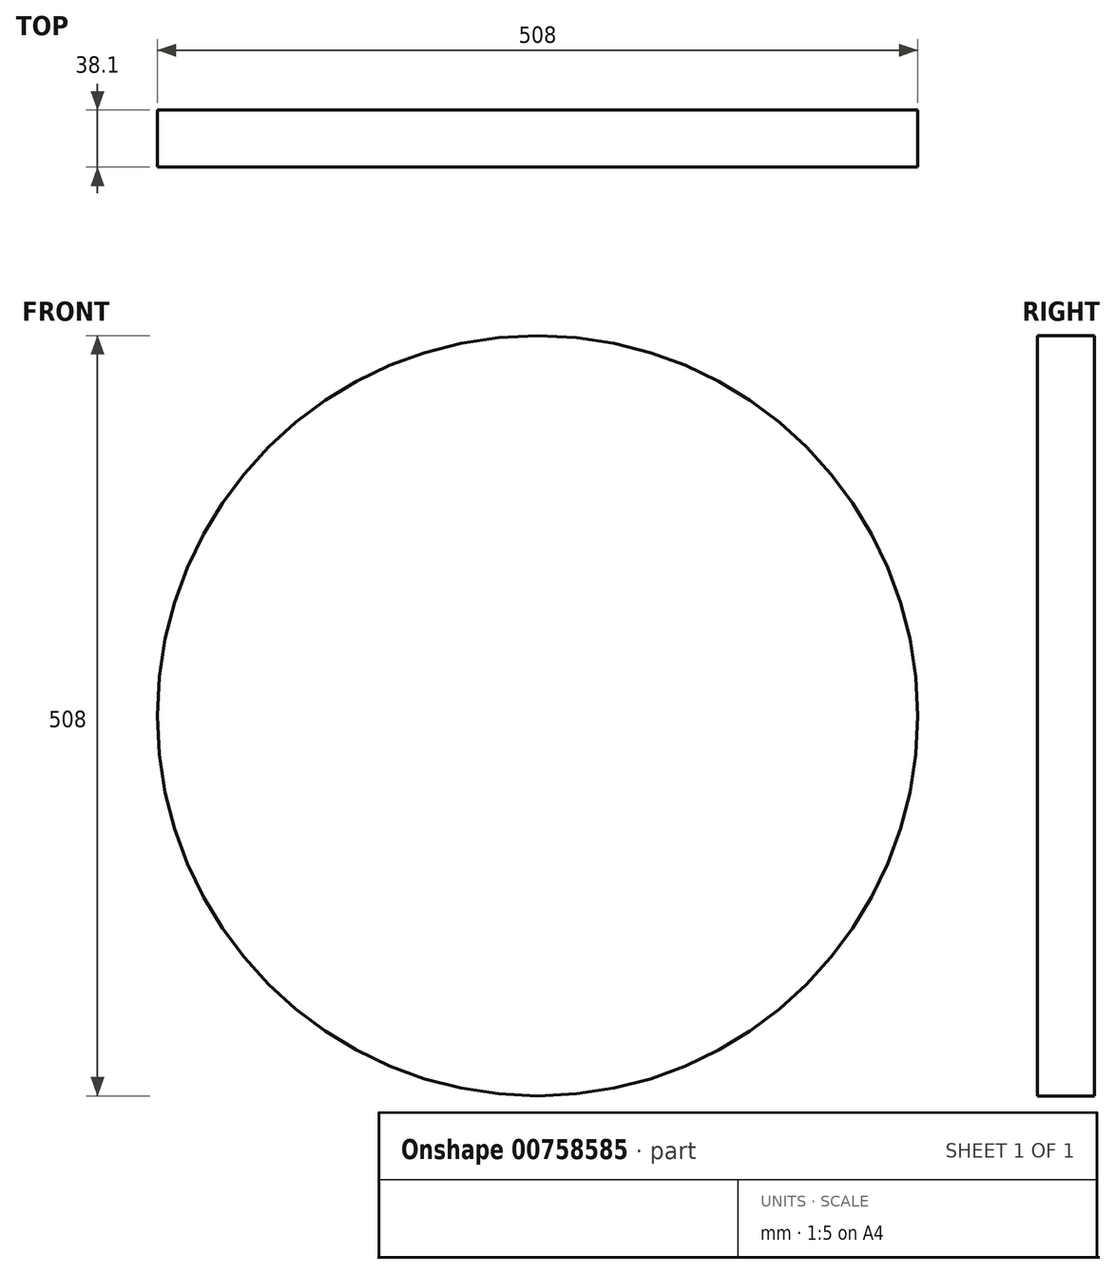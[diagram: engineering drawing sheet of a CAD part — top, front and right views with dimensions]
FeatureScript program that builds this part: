
annotation { "Feature Type Name" : "Feature", "Feature Type Description" : "" }
export const myFeature = defineFeature(function(context is Context, id is Id, definition is map)
    precondition{}
    {
        {
            var Q0;
            Q0=qCreatedBy(makeId("Front.planeOp"),FACE);
            var sketch = newSketch(context, id + "F0", { "sketchPlane" : qUnion([Q0])});
            skCircle(sketch, "E0", {"center": v(0, 0) * mm, "radius": 254 * mm});
            skSolve(sketch);
        }
        {
            var Q0;
            Q0=makeQuery(id+"F0.imprint","IMPRINT",FACE,{"disambiguationData":[TD([[makeQuery(id+"F0.imprint","IMPRINT",EDGE,{"derivedFrom":sQuery(id+"F0.wireOp",EDGE,"E0")}),1.0]])]});
            extrude(context, id + "F1", {"entities" : qUnion([Q0]), "depth" : 38.1 * mm, "offsetDistance" : 25.4 * mm});
        }
    });
